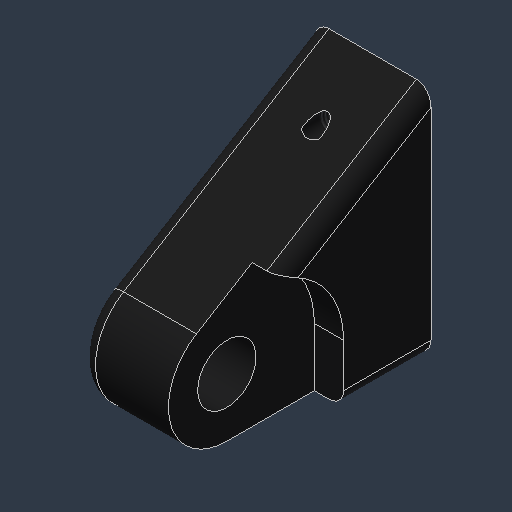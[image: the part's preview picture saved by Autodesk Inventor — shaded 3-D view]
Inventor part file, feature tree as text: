
AUTODESK INVENTOR PART (.ipt)
format: ipt  version: 2024.3 (Build 283343000, 343)  size: 174,592 bytes
history: native  units: mm (DEFAULTED — no unit token found)
features: sketch x4, other x3, extrude x2, hole x2, pattern_linear x1, fillet x1, projected_geometry x1
ambient origin geometry x8: Origin, YZ Plane, XZ Plane, XY Plane, X Axis, Y Axis, Z Axis, Center Point
bodies: Solid1 (feature_tree), Solid1_1 (feature_tree)
feature tree (14):
  other  "MOUNT,SPRING,ELEVATOR.ipt"
  extrude  "Extrusion1"  Depth=12.7mm
  hole  "Hole1"  [1 undecoded]
  extrude  "Extrusion2"  Depth=3.175mm TaperAngle=0.0deg
  hole  "Hole2"  [1 undecoded]
  pattern_linear  "Rectangular Pattern1"  Count1=4 Spacing1=12.7mm
  fillet  "Fillet1"  Radius=3.175mm
  sketch  "Sketch2"  dims[d0=12.7mm d1=50.8mm]
  sketch  "Sketch3"  dims[d2=38.1mm d3=25.4mm d4=0.0mm]
  sketch  "Sketch4"  dims[d5=38.1mm d6=3.175mm d7=0.0mm]
  sketch  "Sketch5"  dims[d8=12.7mm d9=19.05mm d10=9.779mm d11=1.9558mm d12=14.3117mm d13=25.4mm d14=20.594885mm d15=7.9375mm d16=3.9624mm d17=9.652mm d18=9.779mm d19=6.35mm d20=14.3117mm d21=13.6144mm d22=20.594885mm d23=40.0mm d25=12.7mm d26=3.175mm d27=10.0mm]
  projected_geometry  "Projected Loop1"
  other  "Solid1::MOUNT,SPRING,ELEVATOR.ipt"
  other  "TaggingFeature1"
note: 2 required parameter values undecoded (feature->parameter linkage not recoverable at this tier; creation-order binding heuristic only, values carry confidence <= 0.55)
